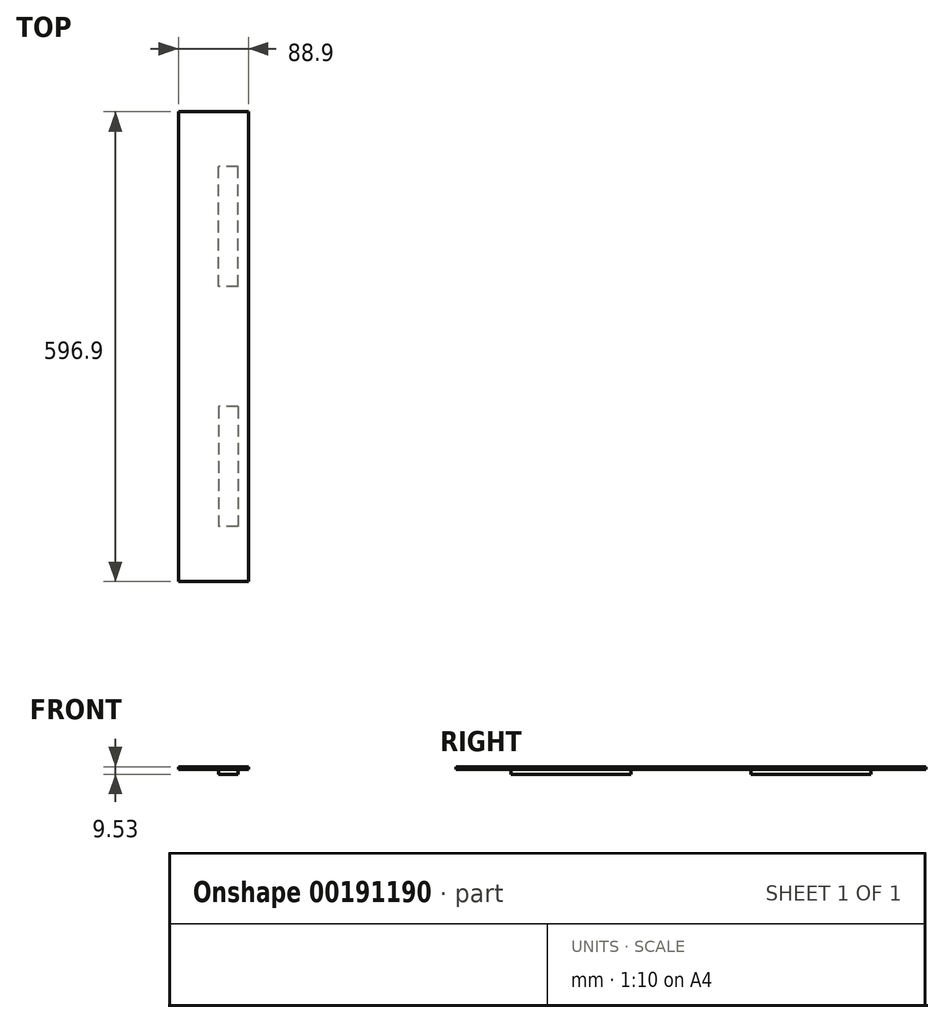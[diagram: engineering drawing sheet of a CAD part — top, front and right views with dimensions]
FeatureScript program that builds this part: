
annotation { "Feature Type Name" : "Feature", "Feature Type Description" : "" }
export const myFeature = defineFeature(function(context is Context, id is Id, definition is map)
    precondition{}
    {
        {
            var Q0;
            Q0=qCreatedBy(makeId("Top.planeOp"),FACE);
            var sketch = newSketch(context, id + "F0", { "sketchPlane" : qUnion([Q0])});
            skLineSegment(sketch, "E0.left", {"start": v(44.45, 298.45) * mm, "end": v(44.45, -298.45) * mm});
            skLineSegment(sketch, "E0.right", {"start": v(-44.45, 298.45) * mm, "end": v(-44.45, -298.45) * mm});
            skPoint(sketch, "E0.middle", {"position": v(0, 0) * mm});
            skPoint(sketch, "E1", {"position": v(44.45, 0) * mm});
            skPoint(sketch, "E2", {"position": v(-44.45, 0) * mm});
            skLineSegment(sketch, "E3", {"start": v(-44.45, -298.45) * mm, "end": v(44.45, -298.45) * mm});
            skLineSegment(sketch, "E4", {"start": v(-44.45, 298.45) * mm, "end": v(44.45, 298.45) * mm});
            skSolve(sketch);
        }
        {
            var Q0;
            Q0 = qSketchRegion(id + "F0", true);
            extrude(context, id + "F1", {"entities" : qUnion([Q0]), "oppositeDirection" : true, "depth" : 3.17 * mm});
        }
        {
            var Q0;
            Q0=makeQuery(id+"F1.opExtrude","CAP_FACE",FACE,{"disambiguationData":[OSD([sQuery(id+"F0.wireOp",EDGE,"E0.bottom"),sQuery(id+"F0.wireOp",EDGE,"E0.top"),sQuery(id+"F0.wireOp",EDGE,"E0.left"),sQuery(id+"F0.wireOp",EDGE,"E0.right")])],"isStart":false});
            var sketch = newSketch(context, id + "F2", { "sketchPlane" : qUnion([Q0])});
            skLineSegment(sketch, "E5.bottom", {"start": v(31.75, 76.2) * mm, "end": v(6.35, 76.2) * mm});
            skLineSegment(sketch, "E5.top", {"start": v(31.75, 228.6) * mm, "end": v(6.35, 228.6) * mm});
            skLineSegment(sketch, "E5.left", {"start": v(31.75, 76.2) * mm, "end": v(31.75, 228.6) * mm});
            skLineSegment(sketch, "E5.right", {"start": v(6.35, 76.2) * mm, "end": v(6.35, 228.6) * mm});
            skPoint(sketch, "E5.middle", {"position": v(19.05, 152.4) * mm});
            skLineSegment(sketch, "E6", {"start": v(-132.32, 0) * mm, "end": v(146.58, 0) * mm, "construction": true});
            skLineSegment(sketch, "E7.MirrorCS", {"start": v(31.75, -76.2) * mm, "end": v(6.35, -76.2) * mm});
            skLineSegment(sketch, "E8.MirrorCS", {"start": v(6.35, -76.2) * mm, "end": v(6.35, -228.6) * mm});
            skLineSegment(sketch, "E9.MirrorCS", {"start": v(31.75, -76.2) * mm, "end": v(31.75, -228.6) * mm});
            skLineSegment(sketch, "E10.MirrorCS", {"start": v(31.75, -228.6) * mm, "end": v(6.35, -228.6) * mm});
            skSolve(sketch);
        }
        {
            var Q0;
            Q0 = qSketchRegion(id + "F2", true);
            extrude(context, id + "F3", {"entities" : qUnion([Q0]), "operationType" : NewBodyOperationType.ADD, "depth" : 6.35 * mm});
        }
    });
